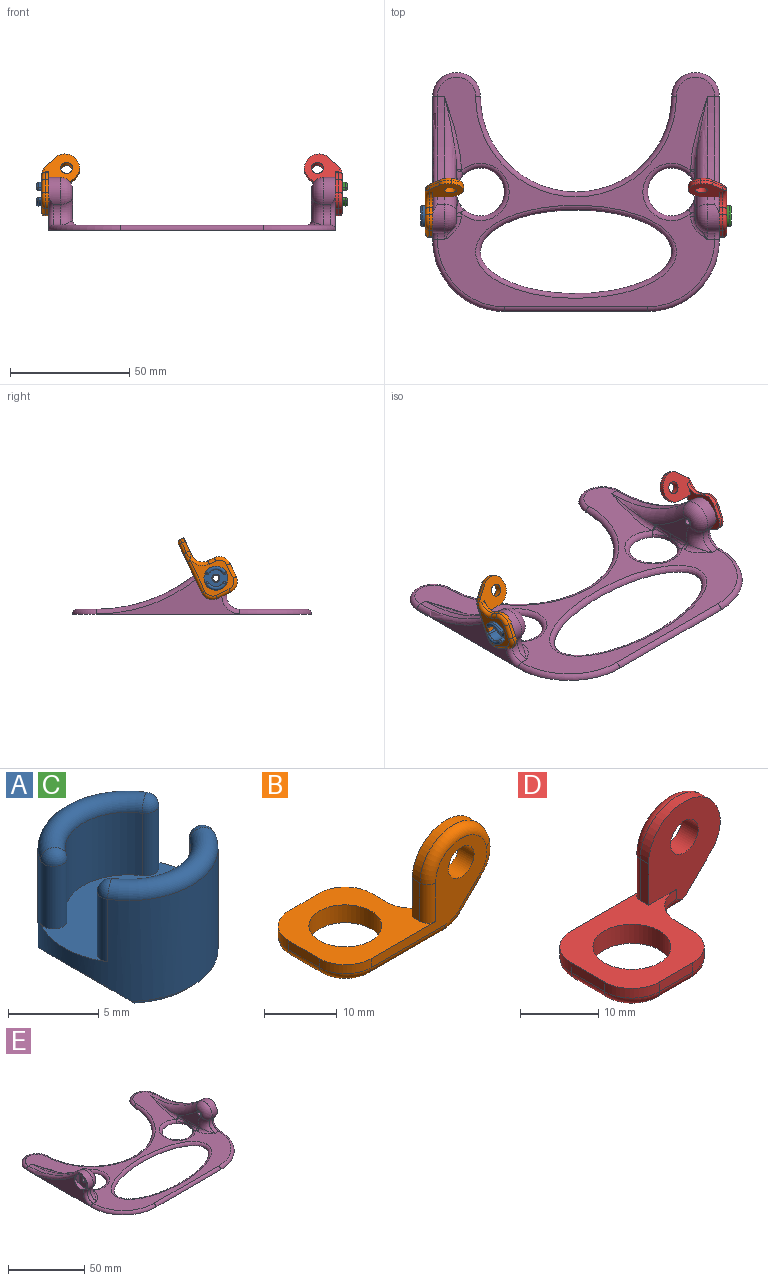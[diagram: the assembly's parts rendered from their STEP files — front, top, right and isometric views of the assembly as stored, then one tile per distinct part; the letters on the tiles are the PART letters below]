
ASSEMBLY  parts=5 mates=5
PART A: 20 faces, bbox 10x10.8x8 mm
  f0: cylinder r=5mm len=10mm, axis (0,0,1), area 150.4mm2, adj f2,f4,f6,f7,f9,f10,f14,f16
  f1: plane 9.2x6mm, normal (0,0,-1), area 41.9mm2, adj f3,f16,f17,f18,f19
  f2: plane 10x7mm, normal (0,0,1), area 40.1mm2, adj f0,f3,f4,f5,f6,f7,f8,f9
  f3: cylinder r=1.7mm len=3.4mm, axis (0,0,1), area 32mm2, adj f1,f2
  f4: cylinder r=0.75mm len=4.25mm, axis (0,0,-1), area 10mm2, adj f0,f2,f5,f15
  f5: cylinder r=3.5mm len=5.94mm, axis (0,0,-1), area 30.1mm2, adj f2,f4,f6,f14
  f6: cylinder r=0.75mm len=4.25mm, axis (0,0,-1), area 10mm2, adj f0,f2,f5,f13
  f7: cylinder r=0.75mm len=4.25mm, axis (0,0,-1), area 10mm2, adj f0,f2,f8,f12
  f8: cylinder r=3.5mm len=5.94mm, axis (0,0,-1), area 30.1mm2, adj f2,f7,f9,f10
  f9: cylinder r=0.75mm len=4.25mm, axis (0,0,-1), area 10mm2, adj f0,f2,f8,f11
  f10: torus R=4.25mm, axis (0,0,1), area 20.3mm2, adj f0,f8,f11,f12
  f11: sphere r=0.75mm, area 1.8mm2, adj f9,f10
  f12: sphere r=0.75mm, area 1.8mm2, adj f7,f10
  f13: sphere r=0.75mm, area 1.8mm2, adj f6,f14
  f14: torus R=4.25mm, axis (0,0,1), area 20.3mm2, adj f0,f5,f13,f15
  f15: sphere r=0.75mm, area 1.8mm2, adj f4,f14
  f16: plane 7.34x2.01mm, normal (0.71,0,-0.71), area 15.5mm2, adj f0,f1,f18,f19
  f17: plane 7.34x2.01mm, normal (-0.71,0,-0.71), area 15.5mm2, adj f0,f1,f18,f19
  f18: cone r=5mm half-angle=45deg, axis (0,0,1), area 4mm2, adj f0,f1,f16,f17
  f19: cone r=5mm half-angle=45deg, axis (0,0,1), area 4mm2, adj f0,f1,f16,f17
PART B: 31 faces, bbox 29.8x16.8x17 mm
  f0: plane 21x16mm, normal (0,0,1), area 167.2mm2, adj f1,f2,f3,f4,f5,f6,f7,f8
  f1: plane 6x1.5mm, normal (-1,0,0), area 9mm2, adj f0,f2,f10,f25
  f2: cylinder r=5mm len=5mm, axis (0,0,-1), area 11.8mm2, adj f0,f1,f3,f23
  f3: plane 6x1.5mm, normal (0,1,0), area 9mm2, adj f0,f2,f4,f21
  f4: cylinder r=5mm len=5mm, axis (0,0,-1), area 11.8mm2, adj f0,f3,f5,f20
  f5: plane 3x1.5mm, normal (1,0,0), area 4.5mm2, adj f0,f4,f6,f19
  f6: cylinder r=5mm len=5mm, axis (0,0,-1), area 11.8mm2, adj f0,f5,f7,f18
  f7: plane 15.14x12.98mm, normal (0,1,0), area 125.2mm2, adj f0,f6,f12,f13,f14,f15,f16,f17
  f8: plane 22.47x13mm, normal (0,-1,0), area 95.7mm2, adj f0,f10,f14,f22,f24,f26,f28,f29
  f9: cylinder r=5mm len=10mm, axis (0,0,-1), area 94.2mm2, adj f0,f11
  f10: cylinder r=5mm len=5mm, axis (0,0,-1), area 11.8mm2, adj f0,f1,f8,f27
  f11: plane 17.72x13mm, normal (0,0,-1), area 91.5mm2, adj f9,f16,f18,f19,f20,f21,f23,f25
  f12: plane 6.5x1.5mm, normal (-1,0,0), area 9.8mm2, adj f0,f7,f13,f22
  f13: cylinder r=6.5mm len=12.8mm, axis (0,-1,0), area 28.2mm2, adj f7,f12,f17,f24
  f14: cylinder r=2.5mm len=5mm, axis (0,-1,0), area 47.1mm2, adj f7,f8
  f15: plane 4.25x4.25mm, normal (0.71,0,-0.71), area 9mm2, adj f7,f16,f17,f28
  f16: cylinder r=5.5mm len=3.89mm, axis (0,1,0), area 4.3mm2, adj f7,f11,f15,f18,f30
  f17: cylinder r=5.5mm len=5.25mm, axis (0,-1,0), area 8.5mm2, adj f7,f13,f15,f26
  f18: torus R=6.5mm, axis (0,0,1), area 20.5mm2, adj f6,f7,f11,f16,f19
  f19: cylinder r=1.5mm len=3mm, axis (0,-1,0), area 7.1mm2, adj f5,f11,f18,f20
  f20: torus R=3.5mm, axis (0,0,1), area 16.5mm2, adj f4,f11,f19,f21
  f21: cylinder r=1.5mm len=6mm, axis (1,0,0), area 14.1mm2, adj f3,f11,f20,f23
  f22: cylinder r=1.5mm len=6.5mm, axis (0,0,-1), area 15.3mm2, adj f0,f8,f12,f24
  f23: torus R=3.5mm, axis (0,0,1), area 16.5mm2, adj f2,f11,f21,f25
  f24: torus R=5mm, axis (0,1,0), area 40.6mm2, adj f8,f13,f22,f26
  f25: cylinder r=1.5mm len=6mm, axis (0,1,0), area 14.1mm2, adj f1,f11,f23,f27
  f26: torus R=4mm, axis (0,1,0), area 12.1mm2, adj f8,f17,f24,f28
  f27: torus R=3.5mm, axis (0,0,1), area 16.5mm2, adj f10,f11,f25,f29
  f28: cylinder r=1.5mm len=5.31mm, axis (-0.71,0,-0.71), area 14.2mm2, adj f8,f15,f26,f30
  f29: cylinder r=1.5mm len=14.22mm, axis (-1,0,0), area 33.5mm2, adj f8,f11,f27,f30
  f30: torus R=4mm, axis (0,1,0), area 9.2mm2, adj f8,f16,f28,f29
PART C: same geometry as A
PART D: 31 faces, bbox 29.8x16.8x17 mm
  f0: plane 21x16mm, normal (0,0,1), area 167.2mm2, adj f1,f2,f3,f4,f5,f6,f7,f8
  f1: plane 6x1.5mm, normal (-1,0,0), area 9mm2, adj f0,f2,f10,f25
  f2: cylinder r=5mm len=5mm, axis (0,0,-1), area 11.8mm2, adj f0,f1,f3,f23
  f3: plane 6x1.5mm, normal (0,-1,0), area 9mm2, adj f0,f2,f4,f21
  f4: cylinder r=5mm len=5mm, axis (0,0,-1), area 11.8mm2, adj f0,f3,f5,f20
  f5: plane 3x1.5mm, normal (1,0,0), area 4.5mm2, adj f0,f4,f6,f19
  f6: cylinder r=5mm len=5mm, axis (0,0,-1), area 11.8mm2, adj f0,f5,f7,f18
  f7: plane 15.14x12.98mm, normal (0,-1,0), area 125.2mm2, adj f0,f6,f12,f13,f14,f15,f16,f17
  f8: plane 22.47x13mm, normal (0,1,0), area 95.7mm2, adj f0,f10,f14,f22,f24,f26,f28,f29
  f9: cylinder r=5mm len=10mm, axis (0,0,-1), area 94.2mm2, adj f0,f11
  f10: cylinder r=5mm len=5mm, axis (0,0,-1), area 11.8mm2, adj f0,f1,f8,f27
  f11: plane 17.72x13mm, normal (0,0,-1), area 91.5mm2, adj f9,f16,f18,f19,f20,f21,f23,f25
  f12: plane 6.5x1.5mm, normal (-1,0,0), area 9.7mm2, adj f0,f7,f13,f22
  f13: cylinder r=6.5mm len=12.8mm, axis (0,1,0), area 28.2mm2, adj f7,f12,f17,f24
  f14: cylinder r=2.5mm len=5mm, axis (0,1,0), area 47.1mm2, adj f7,f8
  f15: plane 4.25x4.25mm, normal (0.71,0,-0.71), area 9mm2, adj f7,f16,f17,f28
  f16: cylinder r=5.5mm len=3.89mm, axis (0,-1,0), area 4.3mm2, adj f7,f11,f15,f18,f30
  f17: cylinder r=5.5mm len=5.25mm, axis (0,1,0), area 8.5mm2, adj f7,f13,f15,f26
  f18: torus R=6.5mm, axis (0,0,1), area 20.5mm2, adj f6,f7,f11,f16,f19
  f19: cylinder r=1.5mm len=3mm, axis (0,1,0), area 7.1mm2, adj f5,f11,f18,f20
  f20: torus R=3.5mm, axis (0,0,1), area 16.5mm2, adj f4,f11,f19,f21
  f21: cylinder r=1.5mm len=6mm, axis (1,0,0), area 14.1mm2, adj f3,f11,f20,f23
  f22: cylinder r=1.5mm len=6.5mm, axis (0,0,-1), area 15.3mm2, adj f0,f8,f12,f24
  f23: torus R=3.5mm, axis (0,0,1), area 16.5mm2, adj f2,f11,f21,f25
  f24: torus R=5mm, axis (0,-1,0), area 40.6mm2, adj f8,f13,f22,f26
  f25: cylinder r=1.5mm len=6mm, axis (0,-1,0), area 14.1mm2, adj f1,f11,f23,f27
  f26: torus R=4mm, axis (0,-1,0), area 12.1mm2, adj f8,f17,f24,f28
  f27: torus R=3.5mm, axis (0,0,1), area 16.5mm2, adj f10,f11,f25,f29
  f28: cylinder r=1.5mm len=5.31mm, axis (-0.71,0,-0.71), area 14.2mm2, adj f8,f15,f26,f30
  f29: cylinder r=1.5mm len=14.22mm, axis (-1,0,0), area 33.5mm2, adj f8,f11,f27,f30
  f30: torus R=4mm, axis (0,-1,0), area 9.2mm2, adj f8,f16,f28,f29
PART E: 63 faces, bbox 127.1x105.5x38.2 mm
  f0: plane 60x17.12mm, normal (1,0,0), area 330.3mm2, adj f5,f6,f53,f58
  f1: plane 60x17.12mm, normal (-1,0,0), area 330.3mm2, adj f5,f18,f57,f61
  f2: plane 118.17x98.17mm, normal (0,0,1), area 2918.5mm2, adj f8,f9,f20,f21,f35,f36,f37,f39
  f3: plane 8.87x8.72mm, normal (1,0,0), area 17.8mm2, adj f6,f10,f53,f58
  f4: plane 8.87x8.72mm, normal (-1,0,0), area 17.8mm2, adj f18,f22,f57,f61
  f5: plane 120.46x100.46mm, normal (0,0,-1), area 5387.5mm2, adj f0,f1,f32,f33,f36,f41,f42,f48
  f6: cylinder r=5.5mm len=11mm, axis (1,0,0), area 80.3mm2, adj f0,f3,f7,f13,f14,f53,f58
  f7: plane 11x7.2mm, normal (1,0,0), area 67.8mm2, adj f6,f12,f13,f14
  f8: cylinder r=5.5mm len=8.8mm, axis (1,0,0), area 36.5mm2, adj f2,f10,f15,f53
  f9: cylinder r=65.5mm len=45.17mm, axis (1,0,0), area 149.5mm2, adj f2,f10,f17,f58
  f10: cylinder r=7mm len=11.83mm, axis (1,0,0), area 95.1mm2, adj f3,f8,f9,f16,f53,f58
  f11: plane 21.37x13mm, normal (-1,0,0), area 117.3mm2, adj f12,f15,f16,f17,f44,f45,f47,f51
  f12: cylinder r=1.3mm len=7mm, axis (1,0,0), area 57.2mm2, adj f7,f11
  f13: plane 8.55x2.14mm, normal (0.71,-0.71,0), area 15.5mm2, adj f6,f7
  f14: plane 8.32x1.9mm, normal (0.71,0.71,0), area 15.5mm2, adj f6,f7
  f15: torus R=10.5mm, axis (1,0,0), area 87.7mm2, adj f8,f11,f16,f46
  f16: torus R=2mm, axis (1,0,0), area 121.1mm2, adj f10,f11,f15,f17
  f17: torus R=70.5mm, axis (1,0,0), area 282mm2, adj f9,f11,f16,f50
  f18: cylinder r=5.5mm len=11mm, axis (-1,0,0), area 80.3mm2, adj f1,f4,f19,f25,f26,f57,f61
  f19: plane 11x7.2mm, normal (-1,0,0), area 67.8mm2, adj f18,f24,f25,f26
  f20: cylinder r=5.5mm len=8.8mm, axis (-1,0,0), area 36.5mm2, adj f2,f22,f27,f57
  f21: cylinder r=65.5mm len=45.17mm, axis (-1,0,0), area 149.5mm2, adj f2,f22,f29,f61
  f22: cylinder r=7mm len=11.83mm, axis (-1,0,0), area 95.1mm2, adj f4,f20,f21,f28,f57,f61
  f23: plane 21.37x13mm, normal (1,0,0), area 117.3mm2, adj f24,f27,f28,f29,f30,f37,f38,f40
  f24: cylinder r=1.3mm len=7mm, axis (-1,0,0), area 57.2mm2, adj f19,f23
  f25: plane 8.55x2.14mm, normal (-0.71,-0.71,0), area 15.5mm2, adj f18,f19
  f26: plane 8.32x1.9mm, normal (-0.71,0.71,0), area 15.5mm2, adj f18,f19
  f27: torus R=10.5mm, axis (-1,0,0), area 87.7mm2, adj f20,f23,f28,f35
  f28: torus R=2mm, axis (-1,0,0), area 121.1mm2, adj f22,f23,f27,f29
  f29: torus R=70.5mm, axis (-1,0,0), area 282mm2, adj f21,f23,f28,f39
  f30: bspline ~8.94x2.08mm, area 15.3mm2, adj f23,f31,f37,f38
  f31: bspline ~8.94x2.78mm, area 11.1mm2, adj f30,f32,f36,f37
  f32: bspline ~7.79x3.33mm, area 12.2mm2, adj f5,f31,f33,f36
  f33: bspline ~7.79x3.33mm, area 12.2mm2, adj f5,f32,f34,f36
  f34: bspline ~8.94x2.78mm, area 11.1mm2, adj f33,f36,f38,f40
  f35: bspline ~11.67x7mm, area 14.1mm2, adj f2,f27,f37
  f36: torus R=12mm, axis (0,0,1), area 155.8mm2, adj f2,f5,f31,f32,f33,f34
  f37: cylinder r=2mm len=2mm, axis (0,1,0), area 3.9mm2, adj f2,f23,f30,f31,f35
  f38: bspline ~8.94x2.08mm, area 15.3mm2, adj f23,f30,f34,f40
  f39: bspline ~32.51x7mm, area 31.8mm2, adj f2,f29,f40
  f40: cylinder r=2mm len=2mm, axis (0,1,0), area 1.6mm2, adj f2,f23,f34,f38,f39
  f41: bspline ~7.79x3.33mm, area 12.2mm2, adj f5,f42,f48,f49
  f42: bspline ~7.79x3.33mm, area 12.2mm2, adj f5,f41,f43,f48
  f43: bspline ~8.94x2.78mm, area 11.1mm2, adj f42,f44,f47,f48
  f44: bspline ~8.94x2.08mm, area 15.3mm2, adj f11,f43,f45,f47
  f45: bspline ~8.94x2.08mm, area 15.3mm2, adj f11,f44,f49,f51
  f46: bspline ~11.67x7mm, area 13.5mm2, adj f2,f15,f47
  f47: cylinder r=2mm len=2mm, axis (0,1,0), area 3.9mm2, adj f2,f11,f43,f44,f46
  f48: torus R=12mm, axis (0,0,1), area 155.8mm2, adj f2,f5,f41,f42,f43,f49
  f49: bspline ~8.94x2.78mm, area 11.1mm2, adj f41,f45,f48,f51
  f50: bspline ~32.51x7mm, area 32mm2, adj f2,f17,f51
  f51: cylinder r=2mm len=2mm, axis (0,1,0), area 1.6mm2, adj f2,f11,f45,f49,f50
  f52: bspline ~84.02x39.01mm, area 603.8mm2, adj f2,f5
  f53: torus R=7.5mm, axis (-1,0,0), area 47.4mm2, adj f0,f3,f6,f8,f10,f54
  f54: torus R=28mm, axis (0,0,1), area 144.5mm2, adj f2,f5,f53,f55
  f55: cylinder r=2mm len=60mm, axis (-1,0,0), area 188.5mm2, adj f2,f5,f54,f56
  f56: torus R=28mm, axis (0,0,1), area 144.5mm2, adj f2,f5,f55,f57
  f57: torus R=7.5mm, axis (-1,0,0), area 47.4mm2, adj f1,f4,f18,f20,f22,f56
  f58: torus R=67.5mm, axis (-1,0,0), area 164.2mm2, adj f0,f3,f6,f9,f10,f59
  f59: torus R=8mm, axis (0,0,1), area 91.5mm2, adj f2,f5,f58,f60
  f60: torus R=42mm, axis (0,0,1), area 402mm2, adj f2,f5,f59,f62
  f61: torus R=67.5mm, axis (-1,0,0), area 164.2mm2, adj f1,f4,f18,f21,f22,f62
  f62: torus R=8mm, axis (0,0,1), area 91.5mm2, adj f2,f5,f60,f61
PLACE A rot(axis=(0.58,-0.58,-0.58),120deg) t=(-60.25,-9.99,4.11)mm
PLACE B rot(axis=(0.7,0.16,0.7),162.2deg) t=(-63.25,25.97,-4.03)mm
PLACE C rot(axis=(0.58,0.58,0.58),120deg) t=(59.75,-9.99,4.11)mm
PLACE D rot(axis=(-0.21,-0.95,0.21),92.7deg) t=(62.75,-6.58,11.35)mm
PLACE E t=(-0.25,-9.99,-10.89)mm fixed
MATE revolute B.f9 <-> A.f0  axis (1,0,0) through (-60.25,-9.99,4.11)mm
MATE fastened C.f0 <-> E.f6  axis (-1,0,0) through (56.75,-9.99,4.11)mm
MATE revolute D.f9 <-> C.f8  axis (-1,0,0) through (59.75,-9.99,4.11)mm
MATE fastened A.f0 <-> E.f18  axis (1,0,0) through (-57.25,-9.99,4.11)mm
MATE planar B.f13 <-> D.f14  axis (0,-0.9,0.43) through (-53.75,0.72,15.09)mm
